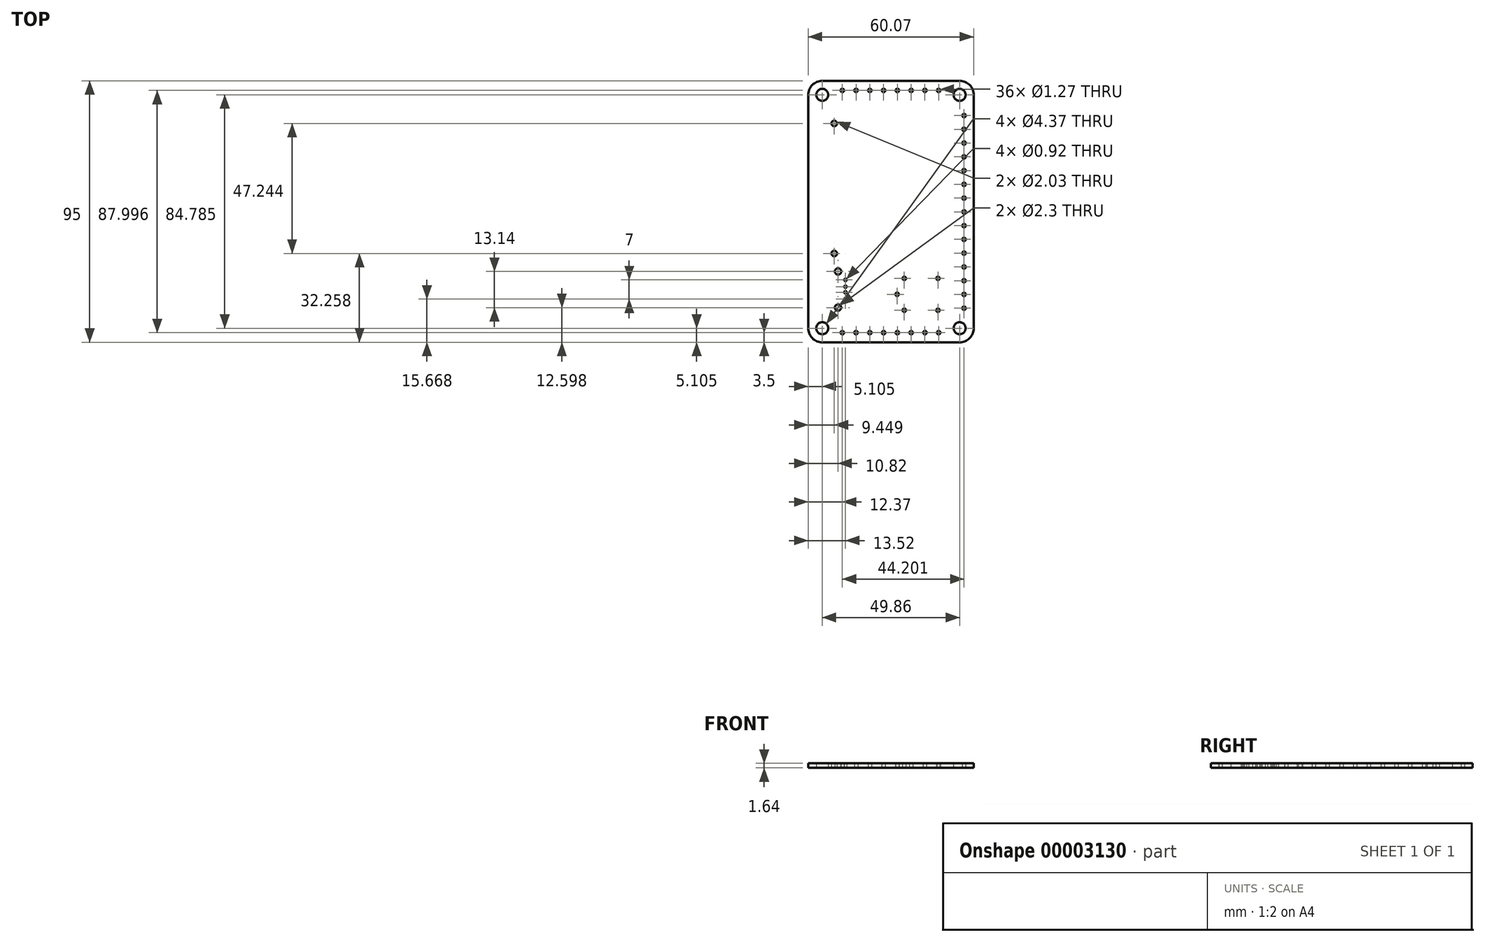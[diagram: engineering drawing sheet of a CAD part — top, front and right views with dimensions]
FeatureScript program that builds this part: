
annotation { "Feature Type Name" : "Feature", "Feature Type Description" : "" }
export const myFeature = defineFeature(function(context is Context, id is Id, definition is map)
    precondition{}
    {
        {
            var Q0;
            Q0=qCreatedBy(makeId("Top.planeOp"),FACE);
            var sketch = newSketch(context, id + "F0", { "sketchPlane" : qUnion([Q0])});
            skLineSegment(sketch, "E0.bottom", {"start": v(5.1, 0) * mm, "end": v(54.97, 0) * mm});
            skLineSegment(sketch, "E0.top", {"start": v(5.1, 95) * mm, "end": v(54.97, 95) * mm});
            skLineSegment(sketch, "E0.left", {"start": v(0, 5.1) * mm, "end": v(0, 89.9) * mm});
            skLineSegment(sketch, "E0.right", {"start": v(60.07, 5.1) * mm, "end": v(60.07, 89.9) * mm});
            skCircle(sketch, "E1", {"center": v(5.1, 89.9) * mm, "radius": 2.18 * mm});
            skCircle(sketch, "E2", {"center": v(54.97, 89.9) * mm, "radius": 2.18 * mm});
            skCircle(sketch, "E3", {"center": v(5.1, 5.1) * mm, "radius": 2.18 * mm});
            skCircle(sketch, "E4", {"center": v(54.97, 5.1) * mm, "radius": 2.18 * mm});
            skPoint(sketch, "E5.visualSharp", {"position": v(0, 95) * mm});
            skArc(sketch, "E5.filletArc", {"start": v(5.1, 95) * mm, "mid": v(1.5, 93.5) * mm, "end": v(0, 89.9) * mm});
            skPoint(sketch, "E6.visualSharp", {"position": v(60.07, 95) * mm});
            skArc(sketch, "E6.filletArc", {"start": v(60.07, 89.9) * mm, "mid": v(58.58, 93.5) * mm, "end": v(54.97, 95) * mm});
            skPoint(sketch, "E7.visualSharp", {"position": v(60.07, 0) * mm});
            skArc(sketch, "E7.filletArc", {"start": v(54.97, 0) * mm, "mid": v(58.58, 1.5) * mm, "end": v(60.07, 5.1) * mm});
            skPoint(sketch, "E8.visualSharp", {"position": v(0, 0) * mm});
            skArc(sketch, "E8.filletArc", {"start": v(0, 5.1) * mm, "mid": v(1.5, 1.5) * mm, "end": v(5.1, 0) * mm});
            skCircle(sketch, "E9", {"center": v(47.12, 11.6) * mm, "radius": 0.64 * mm});
            skCircle(sketch, "E10", {"center": v(47.12, 23.22) * mm, "radius": 0.64 * mm});
            skCircle(sketch, "E11", {"center": v(34.87, 23.22) * mm, "radius": 0.64 * mm});
            skCircle(sketch, "E12", {"center": v(34.87, 11.6) * mm, "radius": 0.64 * mm});
            skCircle(sketch, "E13", {"center": v(32.27, 17.42) * mm, "radius": 0.64 * mm});
            skCircle(sketch, "E14", {"center": v(9.45, 79.5) * mm, "radius": 1.02 * mm});
            skCircle(sketch, "E15", {"center": v(9.45, 32.26) * mm, "radius": 1.02 * mm});
            skCircle(sketch, "E16", {"center": v(12.37, 3.5) * mm, "radius": 0.64 * mm});
            skCircle(sketch, "E17", {"center": v(17.37, 3.5) * mm, "radius": 0.64 * mm});
            skCircle(sketch, "E18", {"center": v(22.37, 3.5) * mm, "radius": 0.64 * mm});
            skCircle(sketch, "E19", {"center": v(27.37, 3.5) * mm, "radius": 0.64 * mm});
            skCircle(sketch, "E20", {"center": v(32.37, 3.5) * mm, "radius": 0.64 * mm});
            skCircle(sketch, "E21", {"center": v(37.37, 3.5) * mm, "radius": 0.64 * mm});
            skCircle(sketch, "E22", {"center": v(42.37, 3.5) * mm, "radius": 0.64 * mm});
            skCircle(sketch, "E23", {"center": v(47.37, 3.5) * mm, "radius": 0.64 * mm});
            skCircle(sketch, "E24", {"center": v(12.37, 91.5) * mm, "radius": 0.64 * mm});
            skCircle(sketch, "E25", {"center": v(17.37, 91.5) * mm, "radius": 0.64 * mm});
            skCircle(sketch, "E26", {"center": v(22.37, 91.5) * mm, "radius": 0.64 * mm});
            skCircle(sketch, "E27", {"center": v(27.37, 91.5) * mm, "radius": 0.64 * mm});
            skCircle(sketch, "E28", {"center": v(32.37, 91.5) * mm, "radius": 0.64 * mm});
            skCircle(sketch, "E29", {"center": v(37.37, 91.5) * mm, "radius": 0.64 * mm});
            skCircle(sketch, "E30", {"center": v(42.37, 91.5) * mm, "radius": 0.64 * mm});
            skCircle(sketch, "E31", {"center": v(47.37, 91.5) * mm, "radius": 0.64 * mm});
            skCircle(sketch, "E32", {"center": v(56.57, 12.37) * mm, "radius": 0.64 * mm});
            skCircle(sketch, "E33", {"center": v(56.57, 17.37) * mm, "radius": 0.64 * mm});
            skCircle(sketch, "E34", {"center": v(56.57, 22.37) * mm, "radius": 0.64 * mm});
            skCircle(sketch, "E35", {"center": v(56.57, 27.37) * mm, "radius": 0.64 * mm});
            skCircle(sketch, "E36", {"center": v(56.57, 32.37) * mm, "radius": 0.64 * mm});
            skCircle(sketch, "E37", {"center": v(56.57, 37.37) * mm, "radius": 0.64 * mm});
            skCircle(sketch, "E38", {"center": v(56.57, 42.37) * mm, "radius": 0.64 * mm});
            skCircle(sketch, "E39", {"center": v(56.57, 47.37) * mm, "radius": 0.64 * mm});
            skCircle(sketch, "E40", {"center": v(56.57, 52.37) * mm, "radius": 0.64 * mm});
            skCircle(sketch, "E41", {"center": v(56.57, 57.37) * mm, "radius": 0.64 * mm});
            skCircle(sketch, "E42", {"center": v(56.57, 62.37) * mm, "radius": 0.64 * mm});
            skCircle(sketch, "E43", {"center": v(56.57, 67.37) * mm, "radius": 0.64 * mm});
            skCircle(sketch, "E44", {"center": v(56.57, 72.37) * mm, "radius": 0.64 * mm});
            skCircle(sketch, "E45", {"center": v(56.57, 77.37) * mm, "radius": 0.64 * mm});
            skCircle(sketch, "E46", {"center": v(56.57, 82.37) * mm, "radius": 0.64 * mm});
            skCircle(sketch, "E47", {"center": v(10.82, 12.6) * mm, "radius": 1.15 * mm});
            skCircle(sketch, "E48", {"center": v(10.82, 25.74) * mm, "radius": 1.15 * mm});
            skCircle(sketch, "E49", {"center": v(13.52, 22.67) * mm, "radius": 0.46 * mm});
            skCircle(sketch, "E50", {"center": v(13.52, 20.17) * mm, "radius": 0.46 * mm});
            skCircle(sketch, "E51", {"center": v(13.52, 18.17) * mm, "radius": 0.46 * mm});
            skCircle(sketch, "E52", {"center": v(13.52, 15.67) * mm, "radius": 0.46 * mm});
            skSolve(sketch);
        }
        {
            var Q0;
            Q0=makeQuery(id+"F0.imprint","IMPRINT",FACE,{"disambiguationData":[TD([[makeQuery(id+"F0.imprint","IMPRINT",EDGE,{"derivedFrom":sQuery(id+"F0.wireOp",EDGE,"E0.bottom")}),1.0]])]});
            extrude(context, id + "F1", {"entities" : qUnion([Q0]), "depth" : 1.64 * mm});
        }
    });
